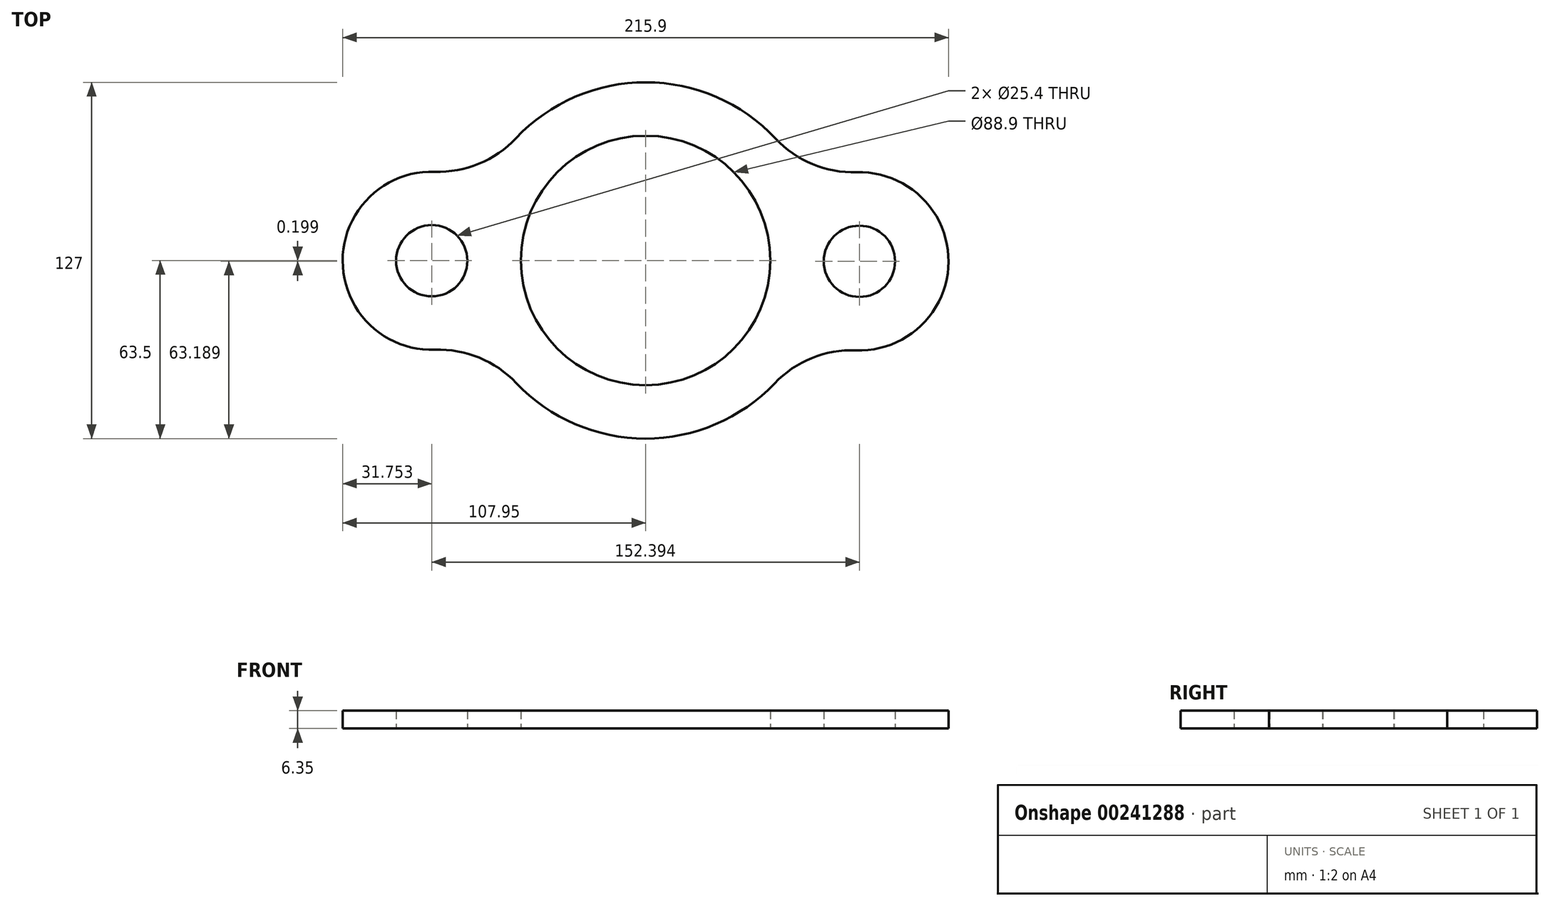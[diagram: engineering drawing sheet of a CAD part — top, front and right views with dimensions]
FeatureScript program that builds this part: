
annotation { "Feature Type Name" : "Feature", "Feature Type Description" : "" }
export const myFeature = defineFeature(function(context is Context, id is Id, definition is map)
    precondition{}
    {
        {
            var Q0;
            Q0=qCreatedBy(makeId("Top.planeOp"),FACE);
            var sketch = newSketch(context, id + "F0", { "sketchPlane" : qUnion([Q0])});
            skArc(sketch, "E0", {"start": v(-63.5, 0.14) * mm, "mid": v(-63.5, -0.1) * mm, "end": v(-63.5, -0.32) * mm});
            skCircle(sketch, "E1", {"center": v(0, 0) * mm, "radius": 44.45 * mm});
            skArc(sketch, "E2", {"start": v(-75.16, 31.62) * mm, "mid": v(-107.95, -0.16) * mm, "end": v(-75.07, -31.84) * mm});
            skArc(sketch, "E3", {"start": v(74.99, -32.04) * mm, "mid": v(107.95, -0.44) * mm, "end": v(75.25, 31.42) * mm});
            skCircle(sketch, "E4", {"center": v(76.2, -0.31) * mm, "radius": 12.7 * mm});
            skCircle(sketch, "E5", {"center": v(-76.2, -0.11) * mm, "radius": 12.7 * mm});
            skArc(sketch, "E6.trimOffspring", {"start": v(-46.07, -43.7) * mm, "mid": v(-0.08, -63.5) * mm, "end": v(45.96, -43.82) * mm});
            skPoint(sketch, "E7.visualSharp", {"position": v(-57.98, 25.9) * mm});
            skArc(sketch, "E7.filletArc", {"start": v(-75.16, 31.62) * mm, "mid": v(-59.4, 34.48) * mm, "end": v(-46.2, 43.56) * mm});
            skArc(sketch, "E8.trimOffspring", {"start": v(46.31, 43.44) * mm, "mid": v(0.08, 63.5) * mm, "end": v(-46.2, 43.56) * mm});
            skArc(sketch, "E9.trimOffspring", {"start": v(63.5, -0.49) * mm, "mid": v(63.5, -0.26) * mm, "end": v(63.5, -0.03) * mm});
            skPoint(sketch, "E10.visualSharp", {"position": v(58.05, 25.74) * mm});
            skArc(sketch, "E10.filletArc", {"start": v(46.31, 43.44) * mm, "mid": v(59.49, 34.32) * mm, "end": v(75.25, 31.42) * mm});
            skPoint(sketch, "E11.visualSharp", {"position": v(57.84, -26.21) * mm});
            skArc(sketch, "E11.filletArc", {"start": v(74.99, -32.04) * mm, "mid": v(59.2, -34.8) * mm, "end": v(45.96, -43.82) * mm});
            skPoint(sketch, "E12.visualSharp", {"position": v(-57.9, -26.06) * mm});
            skArc(sketch, "E12.filletArc", {"start": v(-46.07, -43.7) * mm, "mid": v(-59.3, -34.65) * mm, "end": v(-75.07, -31.84) * mm});
            skSolve(sketch);
        }
        {
            var Q0;
            Q0 = qSketchRegion(id + "F0", true);
            extrude(context, id + "F1", {"entities" : qUnion([Q0]), "depth" : 6.35 * mm});
        }
    });
